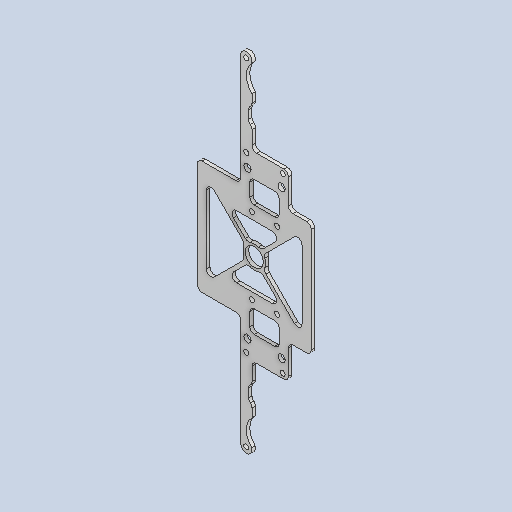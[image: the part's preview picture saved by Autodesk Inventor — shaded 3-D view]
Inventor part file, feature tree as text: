
AUTODESK INVENTOR PART (.ipt)
format: ipt  version: 2025.1 (Build 291241000, 241)  size: 516,608 bytes
history: native  units: mm
features: reference x11, extrude x9, sketch x9, other x8, fillet x6, projected_geometry x1
ambient origin geometry x8: Origin, YZ Plane, XZ Plane, XY Plane, X Axis, Y Axis, Z Axis, Center Point
bodies: Body1 (feature_tree)
feature tree (44):
  other  "ソリッド1"
  extrude  "押し出し1"  Depth=2.2mm
  extrude  "押し出し2"  Depth=2.2mm
  extrude  "押し出し3"  Depth=2.2mm
  fillet  "フィレット1"  Radius=21.0mm
  extrude  "押し出し4"  Depth=80.0mm
  fillet  "フィレット2"  Radius=1.5mm
  extrude  "押し出し6"  Depth=2.2mm
  extrude  "押し出し7"  Depth=2.2mm
  fillet  "フィレット4"  Radius=2.2mm
  fillet  "フィレット5"  Radius=16.0mm
  extrude  "押し出し8"  Depth=8.0mm
  extrude  "押し出し9"  Depth=2.0mm
  fillet  "フィレット6"  [1 undecoded]
  extrude  "押し出し10"  Depth=11.0mm
  fillet  "フィレット7"  Radius=33.5mm
  sketch  "スケッチ1"
  sketch  "スケッチ2"
  sketch  "スケッチ3"
  reference  "参照3"
  reference  "参照4"
  reference  "参照5"
  reference  "参照6"
  sketch  "スケッチ4"
  reference  "参照7"
  reference  "参照8"
  reference  "参照9"
  reference  "参照10"
  sketch  "スケッチ6"
  sketch  "スケッチ7"
  reference  "参照11"
  sketch  "スケッチ8"
  reference  "参照12"
  reference  "参照13"
  sketch  "スケッチ9"
  projected_geometry  "投影ループ1"
  sketch  "スケッチ10"
  other  "<userpath>\Documents\Inventor\Vixen\doutai.iam"
  other  "doutai.iam"
  other  "KRS2500_scale:6"
  other  "02157_SmallDiameterHornB:4"
  other  "02157_SmallDiameterHornB:5"
  other  "KRS2500_scale:5"
  other  "kataue:1"
note: 1 required parameter value undecoded (feature->parameter linkage not recoverable at this tier; creation-order binding heuristic only, values carry confidence <= 0.55)
